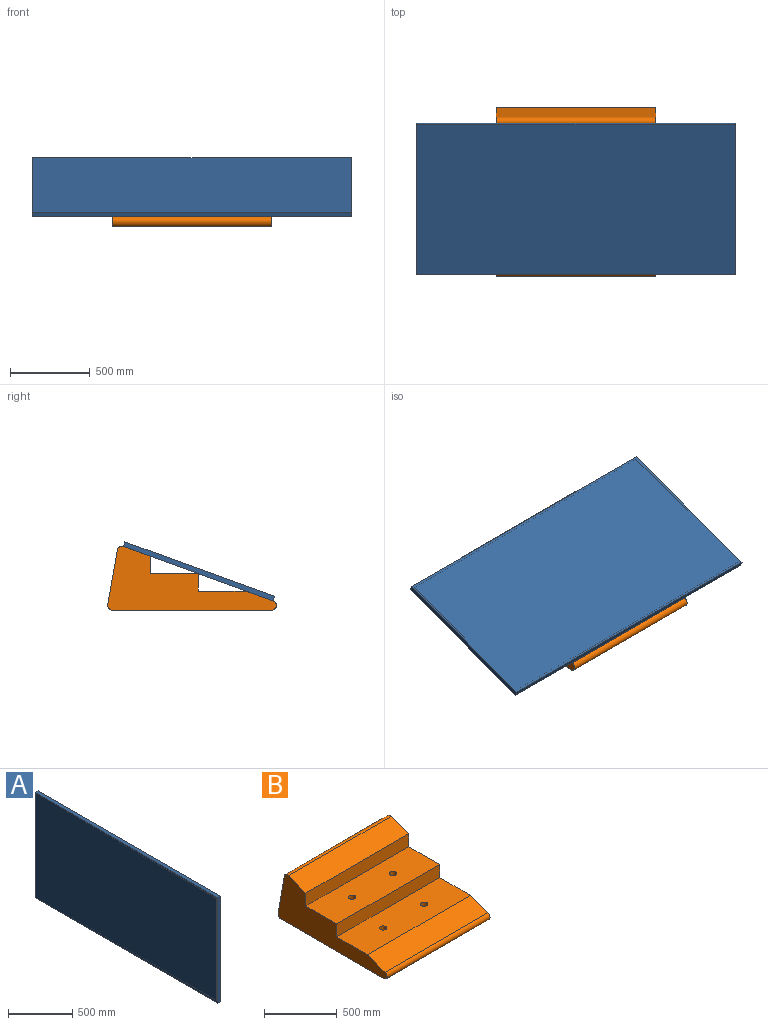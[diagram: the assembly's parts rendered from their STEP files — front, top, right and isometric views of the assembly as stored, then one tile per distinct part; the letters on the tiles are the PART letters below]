
ASSEMBLY  parts=2 mates=1
PART A: 16 faces, bbox 30x2000x1000 mm
  f0: plane 1000x30mm, normal (0,-1,0), area 30000mm2, adj f1,f3,f4,f9
  f1: plane 2000x30mm, normal (0,0,-1), area 60000mm2, adj f0,f2,f4,f9
  f2: plane 1000x30mm, normal (0,1,0), area 30000mm2, adj f1,f3,f4,f9
  f3: plane 2000x30mm, normal (0,0,1), area 60000mm2, adj f0,f2,f4,f9
  f4: plane 2000x1000mm, normal (-1,0,0), area 2000000mm2, adj f0,f1,f2,f3
  f5: plane 1934x1.5mm, normal (0,0,1), area 2901mm2, adj f6,f8,f9,f10
  f6: plane 934x1.5mm, normal (0,1,0), area 1401mm2, adj f5,f7,f9,f10
  f7: plane 1934x1.5mm, normal (0,0,-1), area 2901mm2, adj f6,f8,f9,f10
  f8: plane 934x1.5mm, normal (0,-1,0), area 1401mm2, adj f5,f7,f9,f10
  f9: plane 2000x1000mm, normal (1,0,0), area 193644mm2, adj f0,f1,f2,f3,f5,f6,f7,f8
  f10: plane 1970x970mm, normal (-1,0,0), area 104544mm2, adj f5,f6,f7,f8,f12,f13,f14,f15
  f11: plane 1970x970mm, normal (1,0,0), area 1910900mm2, adj f12,f13,f14,f15
  f12: plane 970x23.5mm, normal (0,-1,0), area 22795mm2, adj f10,f11,f13,f15
  f13: plane 1970x23.5mm, normal (0,0,-1), area 46295mm2, adj f10,f11,f12,f14
  f14: plane 970x23.5mm, normal (0,1,0), area 22795mm2, adj f10,f11,f13,f15
  f15: plane 1970x23.5mm, normal (0,0,1), area 46295mm2, adj f10,f11,f12,f14
PART B: 17 faces, bbox 1000x1060x402 mm
  f0: plane 1000x169.85mm, normal (0,-0.34,0.94), area 180746.7mm2, adj f1,f10,f11,f12
  f1: cylinder r=30mm len=1000mm, axis (-1,0,0), area 83775.8mm2, adj f0,f2,f11,f12
  f2: plane 1000x1000mm, normal (0,0,-1), area 992146mm2, adj f1,f3,f11,f12,f13,f14,f15,f16
  f3: cylinder r=30mm len=1000mm, axis (-1,0,0), area 52359.9mm2, adj f2,f4,f11,f12
  f4: plane 1000x342.02mm, normal (0,0.98,0.17), area 347296.4mm2, adj f3,f5,f11,f12
  f5: cylinder r=30mm len=1000mm, axis (-1,0,0), area 52359.9mm2, adj f4,f6,f11,f12
  f6: plane 1000x169.85mm, normal (0,-0.34,0.94), area 180746.7mm2, adj f5,f7,f11,f12
  f7: plane 1000x109.19mm, normal (0,-1,0), area 109191.1mm2, adj f6,f8,f11,f12
  f8: plane 1000x300mm, normal (0,0,1), area 296073mm2, adj f7,f9,f11,f12,f15,f16
  f9: plane 1000x109.19mm, normal (0,-1,0), area 109191.1mm2, adj f8,f10,f11,f12
  f10: plane 1000x300mm, normal (0,0,1), area 296073mm2, adj f0,f9,f11,f12,f13,f14
  f11: plane 1060x402.02mm, normal (1,0,0), area 211499.1mm2, adj f0,f1,f2,f3,f4,f5,f6,f7
  f12: plane 1060x402.02mm, normal (-1,0,0), area 211499.1mm2, adj f0,f1,f2,f3,f4,f5,f6,f7
  f13: cylinder r=25mm len=120.01mm, axis (0,0,1), area 18851.1mm2, adj f2,f10
  f14: cylinder r=25mm len=120.01mm, axis (0,0,1), area 18851.1mm2, adj f2,f10
  f15: cylinder r=25mm len=229.2mm, axis (0,0,1), area 36002.8mm2, adj f2,f8
  f16: cylinder r=25mm len=229.2mm, axis (0,0,1), area 36002.8mm2, adj f2,f8
PLACE A rot(axis=(-0.5,0.5,0.71),109.2deg) t=(1528.2,-54.01,125.17)mm
PLACE B t=(28.2,-205.85,37.98)mm fixed
MATE planar A.f9 <-> B.f0  axis (0,0.34,-0.94) through (528.2,426.1,267.99)mm
